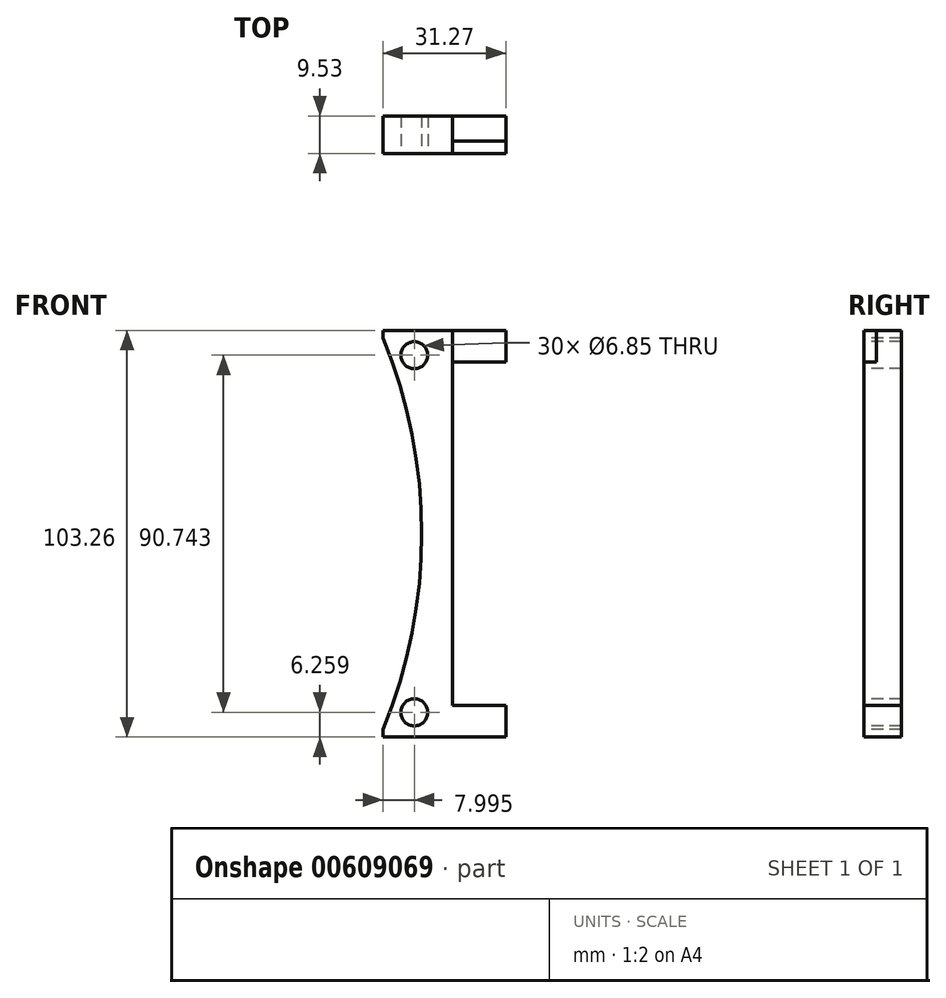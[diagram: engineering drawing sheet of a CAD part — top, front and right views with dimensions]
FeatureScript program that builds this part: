
annotation { "Feature Type Name" : "Feature", "Feature Type Description" : "" }
export const myFeature = defineFeature(function(context is Context, id is Id, definition is map)
    precondition{}
    {
        {
            var Q0;
            Q0=qCreatedBy(makeId("Front.planeOp"),FACE);
            var sketch = newSketch(context, id + "F0", { "sketchPlane" : qUnion([Q0])});
            skLineSegment(sketch, "E0.bottom", {"start": v(24.51, -51.63) * mm, "end": v(-24.51, -51.63) * mm});
            skLineSegment(sketch, "E0.top", {"start": v(24.51, 51.63) * mm, "end": v(-24.51, 51.63) * mm});
            skLineSegment(sketch, "E0.left", {"start": v(24.51, -51.63) * mm, "end": v(24.51, 51.63) * mm});
            skLineSegment(sketch, "E0.right", {"start": v(-24.51, -51.63) * mm, "end": v(-24.51, 51.63) * mm});
            skPoint(sketch, "E0.middle", {"position": v(0, 0) * mm});
            skLineSegment(sketch, "E1.bottom", {"start": v(-6.78, 43.63) * mm, "end": v(6.78, 43.63) * mm});
            skLineSegment(sketch, "E1.top", {"start": v(-6.78, -43.63) * mm, "end": v(6.78, -43.63) * mm});
            skLineSegment(sketch, "E1.left", {"start": v(-6.78, 43.63) * mm, "end": v(-6.78, -43.63) * mm});
            skLineSegment(sketch, "E1.right", {"start": v(6.78, 43.63) * mm, "end": v(6.78, -43.63) * mm});
            skCircle(sketch, "E2", {"center": v(-144.8, 0) * mm, "radius": 130.18 * mm});
            skCircle(sketch, "E3.MirrorC", {"center": v(144.8, 0) * mm, "radius": 130.18 * mm});
            skCircle(sketch, "E4", {"center": v(-16.51, -45.37) * mm, "radius": 3.42 * mm});
            skCircle(sketch, "E5.MirrorC", {"center": v(-16.51, 45.37) * mm, "radius": 3.42 * mm});
            skCircle(sketch, "E6.MirrorC", {"center": v(16.51, 45.37) * mm, "radius": 3.42 * mm});
            skCircle(sketch, "E7.MirrorC", {"center": v(16.51, -45.37) * mm, "radius": 3.42 * mm});
            skLineSegment(sketch, "E8.bottom", {"start": v(-6.78, -43.63) * mm, "end": v(6.76, -43.63) * mm});
            skLineSegment(sketch, "E8.top", {"start": v(-6.78, -51.63) * mm, "end": v(6.76, -51.63) * mm});
            skLineSegment(sketch, "E8.left", {"start": v(-6.78, -43.63) * mm, "end": v(-6.78, -51.63) * mm});
            skLineSegment(sketch, "E8.right", {"start": v(6.76, -43.63) * mm, "end": v(6.76, -51.63) * mm});
            skLineSegment(sketch, "E9.MirrorCS", {"start": v(-6.78, 43.63) * mm, "end": v(-6.78, 51.63) * mm});
            skLineSegment(sketch, "E10.MirrorCS", {"start": v(6.76, 43.63) * mm, "end": v(6.76, 51.63) * mm});
            skLineSegment(sketch, "E11.MirrorCS", {"start": v(-6.78, 51.63) * mm, "end": v(6.76, 51.63) * mm});
            skSolve(sketch);
        }
        {
            var Q0;
            Q0=makeQuery(id+"F0.imprint","IMPRINT",FACE,{"disambiguationData":[TD([[makeQuery(id+"F0.imprint","IMPRINT",EDGE,{"derivedFrom":sQuery(id+"F0.wireOp",EDGE,"E1.left")}),-1.0]])]});
            var Q1;
            Q1=makeQuery(id+"F0.imprint","IMPRINT",FACE,{"disambiguationData":[TD([[makeQuery(id+"F0.imprint","IMPRINT",EDGE,{"derivedFrom":sQuery(id+"F0.wireOp",EDGE,"E1.top")}),-1.0]])]});
            extrude(context, id + "F1", {"entities" : qUnion([Q0, Q1]), "oppositeDirection" : true, "depth" : 9.52 * mm, "offsetDistance" : 25.4 * mm});
        }
        {
            var Q0;
            Q0=makeQuery(id+"F0.imprint","IMPRINT",FACE,{"disambiguationData":[TD([[makeQuery(id+"F0.imprint","IMPRINT",EDGE,{"derivedFrom":sQuery(id+"F0.wireOp",EDGE,"E8.bottom")}),-1.0]])]});
            var Q1;
            {var subQ0=sQuery(id+"F0.wireOp",EDGE,"E9.MirrorCS");Q1=makeQuery(id+"F0.imprint","IMPRINT",FACE,{"disambiguationData":[TD([[makeQuery(id+"F0.imprint","IMPRINT",EDGE,{"derivedFrom":subQ0}),-1.0]])]});}
            extrude(context, id + "F2", {"entities" : qUnion([Q0, Q1]), "oppositeDirection" : true, "depth" : 3.17 * mm, "offsetDistance" : 25.4 * mm});
        }
    });
